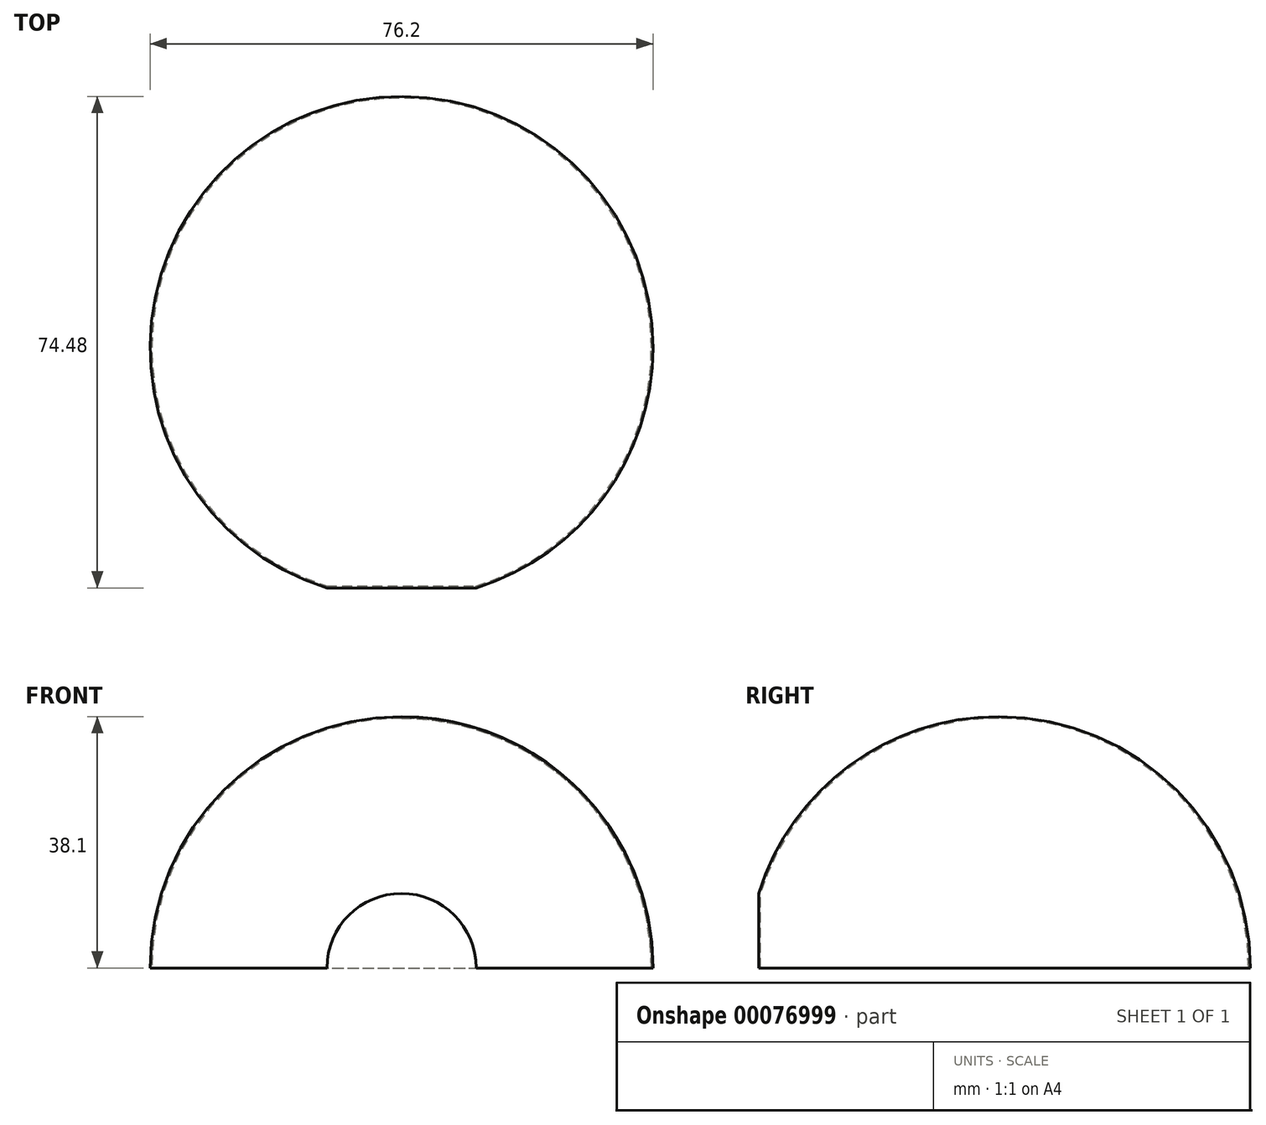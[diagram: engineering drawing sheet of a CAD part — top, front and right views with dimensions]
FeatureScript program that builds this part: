
annotation { "Feature Type Name" : "Feature", "Feature Type Description" : "" }
export const myFeature = defineFeature(function(context is Context, id is Id, definition is map)
    precondition{}
    {
        {
            var Q0;
            Q0=qCreatedBy(makeId("Front.planeOp"),FACE);
            var sketch = newSketch(context, id + "F0", { "sketchPlane" : qUnion([Q0])});
            skArc(sketch, "E0", {"start": v(0, 38.1) * mm, "mid": v(26.94, 26.94) * mm, "end": v(38.1, 0) * mm});
            skArc(sketch, "E1.0", {"start": v(0, 37.85) * mm, "mid": v(26.76, 26.76) * mm, "end": v(37.85, 0) * mm});
            skLineSegment(sketch, "E2", {"start": v(0, 38.1) * mm, "end": v(0, 37.85) * mm});
            skLineSegment(sketch, "E3", {"start": v(37.85, 0) * mm, "end": v(38.1, 0) * mm});
            skSolve(sketch);
        }
        {
            var Q0;
            Q0=qCreatedBy(makeId("Top.planeOp"),FACE);
            var sketch = newSketch(context, id + "F1", { "sketchPlane" : qUnion([Q0])});
            skCircle(sketch, "E4", {"center": v(0, 0) * mm, "radius": 38.1 * mm});
            skSolve(sketch);
        }
        {
            var Q0;
            Q0 = qSketchRegion(id + "F0", true);
            var Q1;
            Q1=sQuery(id+"F1.wireOp",EDGE,"E4");
            revolve(context, id + "F2", {"entities" : qUnion([Q0]), "axis" : qUnion([Q1]), "revolveType" : RevolveType.FULL});
        }
        {
            var Q0;
            Q0=qCreatedBy(makeId("Front.planeOp"),FACE);
            cPlane(context, id + "F3", {"entities" : qUnion([Q0]), "cplaneType" : CPlaneType.OFFSET, "offset" : (1.5 - (.15 / 2)) * mm, "width" : 152.4 * mm, "height" : 152.4 * mm});
        }
        {
            var Q0;
            Q0=qCreatedBy(id+"F3.planeOp",FACE);
            var sketch = newSketch(context, id + "F4", { "sketchPlane" : qUnion([Q0])});
            skArc(sketch, "E5", {"start": v(-11.3, 0) * mm, "mid": v(0, 11.3) * mm, "end": v(11.3, 0) * mm});
            skLineSegment(sketch, "E6", {"start": v(-11.3, 0) * mm, "end": v(11.3, 0) * mm});
            skSolve(sketch);
        }
        {
            var Q0;
            Q0 = qSketchRegion(id + "F4", true);
            extrude(context, id + "F5", {"entities" : qUnion([Q0]), "operationType" : NewBodyOperationType.REMOVE, "endBound" : BoundingType.THROUGH_ALL, "depth" : 25.4 * mm});
        }
        {
            var Q0;
            Q0=qCreatedBy(makeId("Front.planeOp"),FACE);
            cPlane(context, id + "F6", {"entities" : qUnion([Q0]), "cplaneType" : CPlaneType.OFFSET, "offset" : 40.64 * mm, "oppositeDirection" : true, "width" : 152.4 * mm, "height" : 152.4 * mm});
        }
    });
